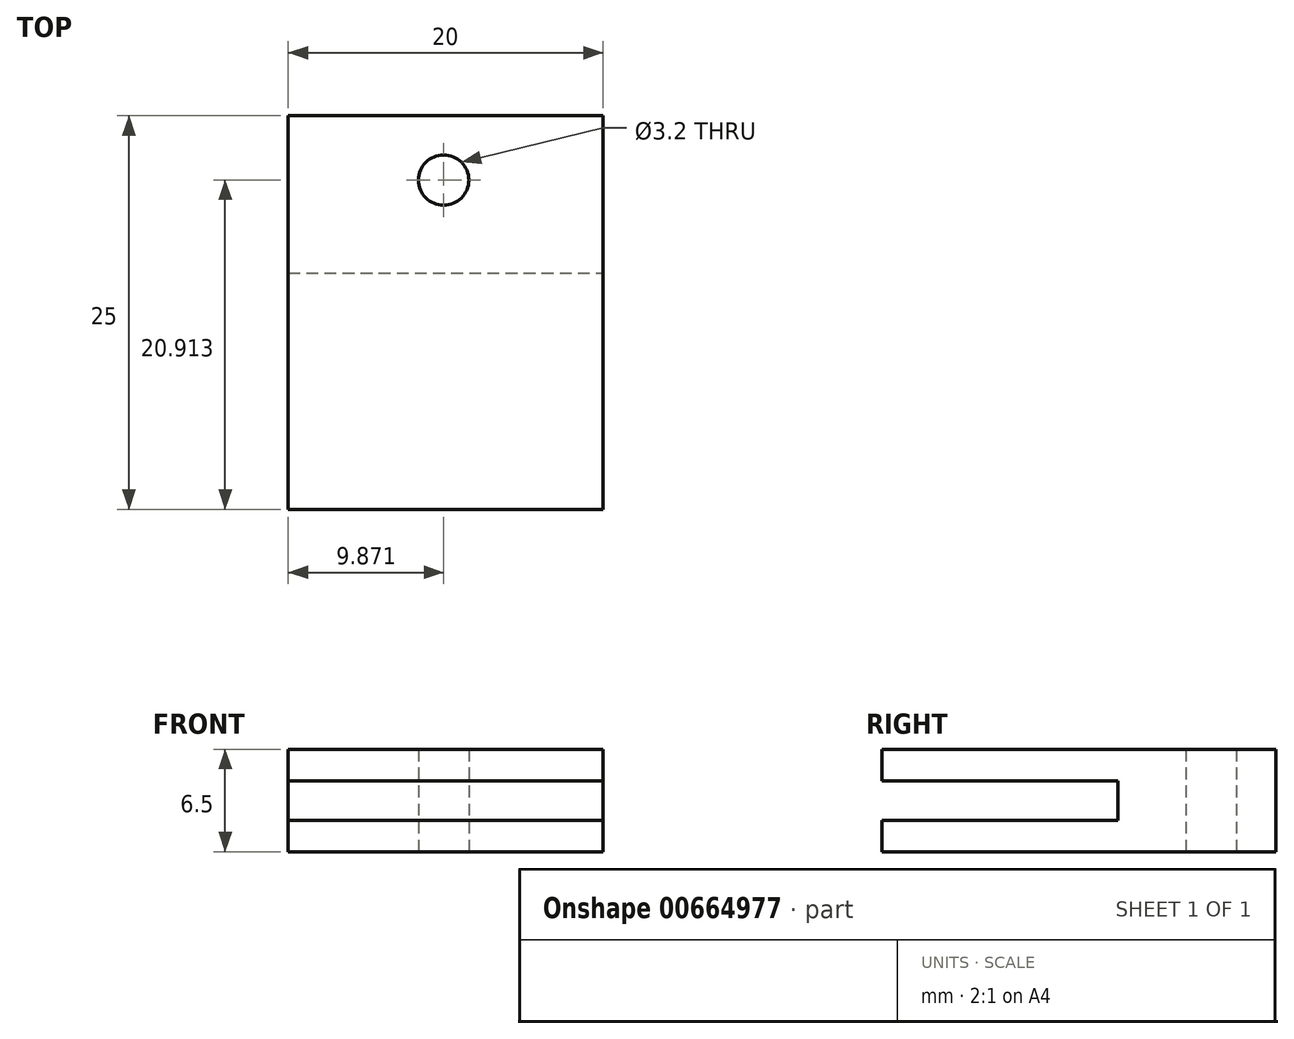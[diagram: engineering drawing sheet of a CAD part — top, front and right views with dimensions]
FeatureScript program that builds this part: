
annotation { "Feature Type Name" : "Feature", "Feature Type Description" : "" }
export const myFeature = defineFeature(function(context is Context, id is Id, definition is map)
    precondition{}
    {
        {
            var Q0;
            Q0=qCreatedBy(makeId("Right.planeOp"),FACE);
            var sketch = newSketch(context, id + "F0", { "sketchPlane" : qUnion([Q0])});
            skLineSegment(sketch, "E0.bottom", {"start": v(-21.63, 34.13) * mm, "end": v(3.37, 34.13) * mm});
            skLineSegment(sketch, "E0.top", {"start": v(-21.63, 34.32) * mm, "end": v(3.37, 34.32) * mm});
            skLineSegment(sketch, "E0.left", {"start": v(-21.63, 34.13) * mm, "end": v(-21.63, 34.32) * mm});
            skLineSegment(sketch, "E0.right", {"start": v(3.37, 34.13) * mm, "end": v(3.37, 34.32) * mm});
            skLineSegment(sketch, "E1", {"start": v(-21.63, 34.13) * mm, "end": v(-21.63, 32.13) * mm});
            skLineSegment(sketch, "E2", {"start": v(-21.63, 32.13) * mm, "end": v(-6.63, 32.13) * mm});
            skLineSegment(sketch, "E3", {"start": v(-6.63, 32.13) * mm, "end": v(-6.63, 29.63) * mm});
            skLineSegment(sketch, "E4", {"start": v(-6.63, 29.63) * mm, "end": v(-21.63, 29.63) * mm});
            skLineSegment(sketch, "E5", {"start": v(-21.63, 29.63) * mm, "end": v(-21.63, 27.63) * mm});
            skLineSegment(sketch, "E6", {"start": v(-21.63, 27.63) * mm, "end": v(3.37, 27.63) * mm});
            skLineSegment(sketch, "E7", {"start": v(3.37, 34.13) * mm, "end": v(3.37, 27.63) * mm});
            skSolve(sketch);
        }
        {
            var Q0;
            Q0=makeQuery(id+"F0.imprint","IMPRINT",FACE,{"disambiguationData":[TD([[makeQuery(id+"F0.imprint","IMPRINT",EDGE,{"derivedFrom":sQuery(id+"F0.wireOp",EDGE,"E0.bottom")}),-1.0]])]});
            extrude(context, id + "F1", {"entities" : qUnion([Q0]), "oppositeDirection" : true, "depth" : 20 * mm, "offsetDistance" : 25 * mm});
        }
        {
            var Q0;
            Q0=makeQuery(id+"F1.opExtrude","SWEPT_FACE",FACE,{"disambiguationData":[OSD([sQuery(id+"F0.wireOp",EDGE,"E6")])]});
            var sketch = newSketch(context, id + "F2", { "sketchPlane" : qUnion([Q0])});
            skCircle(sketch, "E8", {"center": v(-10.13, 0.72) * mm, "radius": 1.6 * mm});
            skSolve(sketch);
        }
        {
            var Q0;
            Q0 = qSketchRegion(id + "F2", true);
            extrude(context, id + "F3", {"entities" : qUnion([Q0]), "operationType" : NewBodyOperationType.REMOVE, "oppositeDirection" : true, "depth" : 6.5 * mm, "offsetDistance" : 25 * mm});
        }
    });
